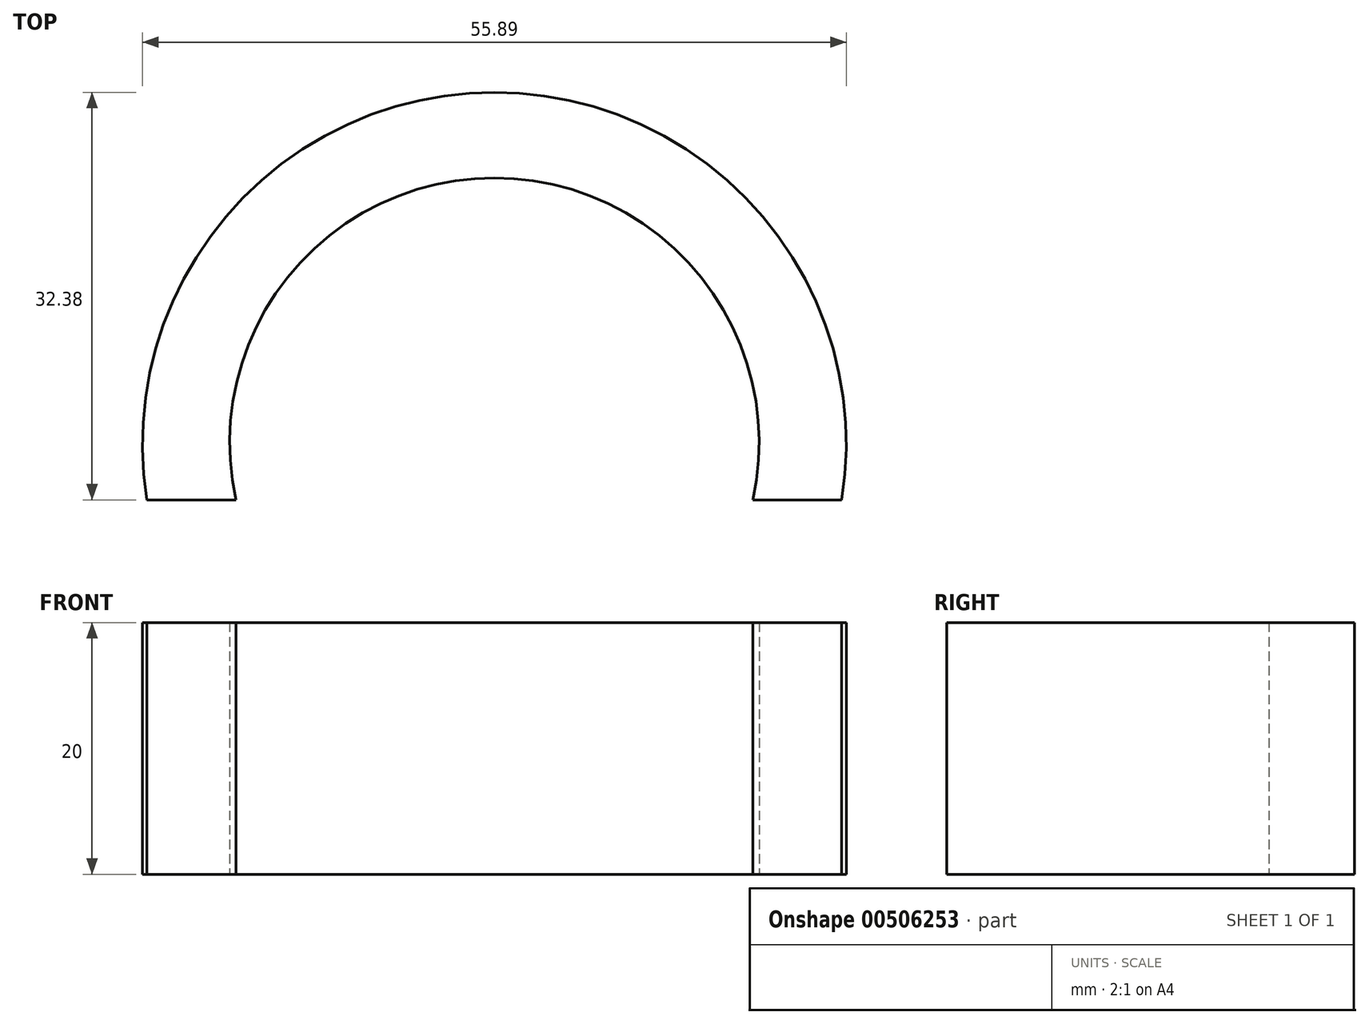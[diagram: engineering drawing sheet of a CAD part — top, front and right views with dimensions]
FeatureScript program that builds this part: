
annotation { "Feature Type Name" : "Feature", "Feature Type Description" : "" }
export const myFeature = defineFeature(function(context is Context, id is Id, definition is map)
    precondition{}
    {
        {
            var Q0;
            Q0=qCreatedBy(makeId("Top.planeOp"),FACE);
            var sketch = newSketch(context, id + "F0", { "sketchPlane" : qUnion([Q0])});
            skArc(sketch, "E0", {"start": v(76, 0) * mm, "mid": v(48.4, 32.38) * mm, "end": v(20.81, 0) * mm});
            skArc(sketch, "E1", {"start": v(68.93, 0) * mm, "mid": v(48.4, 25.58) * mm, "end": v(27.88, 0) * mm});
            skLineSegment(sketch, "E2", {"start": v(27.88, 0) * mm, "end": v(20.81, 0) * mm});
            skLineSegment(sketch, "E3", {"start": v(76, 0) * mm, "end": v(68.93, 0) * mm});
            skSolve(sketch);
        }
        {
            var Q0;
            Q0=makeQuery(id+"F0.imprint","IMPRINT",FACE,{"disambiguationData":[TD([[makeQuery(id+"F0.imprint","IMPRINT",EDGE,{"derivedFrom":sQuery(id+"F0.wireOp",EDGE,"E0")}),1.0]])]});
            extrude(context, id + "F1", {"entities" : qUnion([Q0]), "depth" : 20 * mm});
        }
    });
